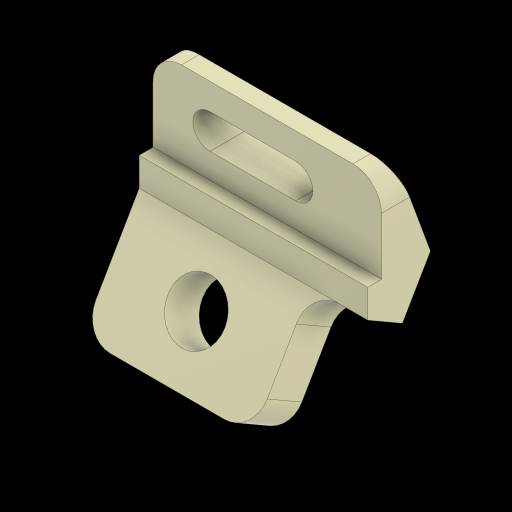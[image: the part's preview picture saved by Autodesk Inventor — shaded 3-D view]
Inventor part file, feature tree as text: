
AUTODESK INVENTOR PART (.ipt)
format: ipt  version: 2024 (Build 280153000, 153)  size: 193,536 bytes
history: native  units: in
note: dims shown in document units (in); Inventor stores cm internally (conversion verified against a paired STEP export)
features: extrude x3, sketch x3, fillet x1
ambient origin geometry x8: Origin, YZ Plane, XZ Plane, XY Plane, X Axis, Y Axis, Z Axis, Center Point
bodies: Solid1 (feature_tree)
feature tree (7):
  extrude  "MAIN BODY"  Depth=0.35in
  extrude  "SLOT CUTOUT"  Depth=0.75in
  extrude  "CIRC AND RECT CUTOUT"  Depth=0.25in
  fillet  ".25 filliets"  Radius=0.25in
  sketch  "Sketch1"  dims[d0=1.5in d1=0.35in]
  sketch  "Sketch2"  dims[d2=30.0deg d3=0.75in]
  sketch  "Sketch3"  dims[d5=0.12in d6=0.1374in d7=0.25in d9=2.0in d10=0.0in d11=0.3in d12=0.75in d13=0.5in d15=0.37in d16=0.0in d17=0.0in d18=0.5in d19=0.75in d20=0.5in d21=1.5in d22=0.0in d23=0.0in d24=0.25in]
